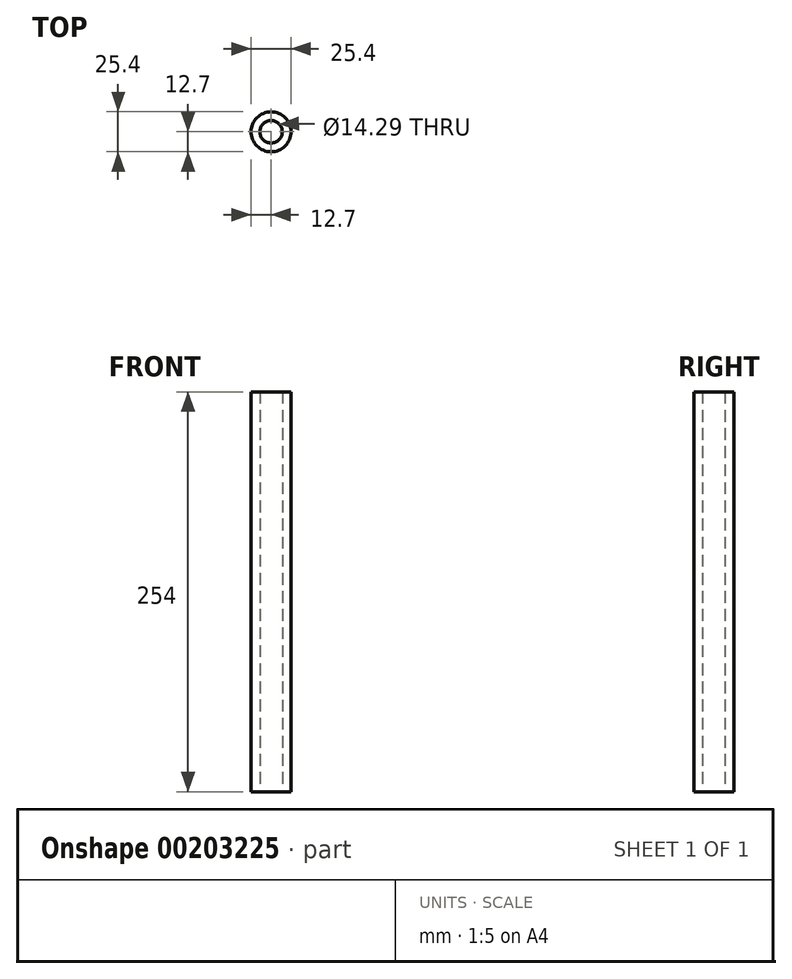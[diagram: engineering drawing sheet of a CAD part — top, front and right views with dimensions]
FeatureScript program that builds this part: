
annotation { "Feature Type Name" : "Feature", "Feature Type Description" : "" }
export const myFeature = defineFeature(function(context is Context, id is Id, definition is map)
    precondition{}
    {
        {
            var Q0;
            Q0=qCreatedBy(makeId("Top.planeOp"),FACE);
            var sketch = newSketch(context, id + "F0", { "sketchPlane" : qUnion([Q0])});
            skCircle(sketch, "E0", {"center": v(0, 0) * mm, "radius": 7.14 * mm});
            skCircle(sketch, "E1", {"center": v(0, 0) * mm, "radius": 12.7 * mm});
            skSolve(sketch);
        }
        {
            var Q0;
            Q0 = qSketchRegion(id + "F0", true);
            extrude(context, id + "F1", {"entities" : qUnion([Q0]), "depth" : 254 * mm});
        }
    });
